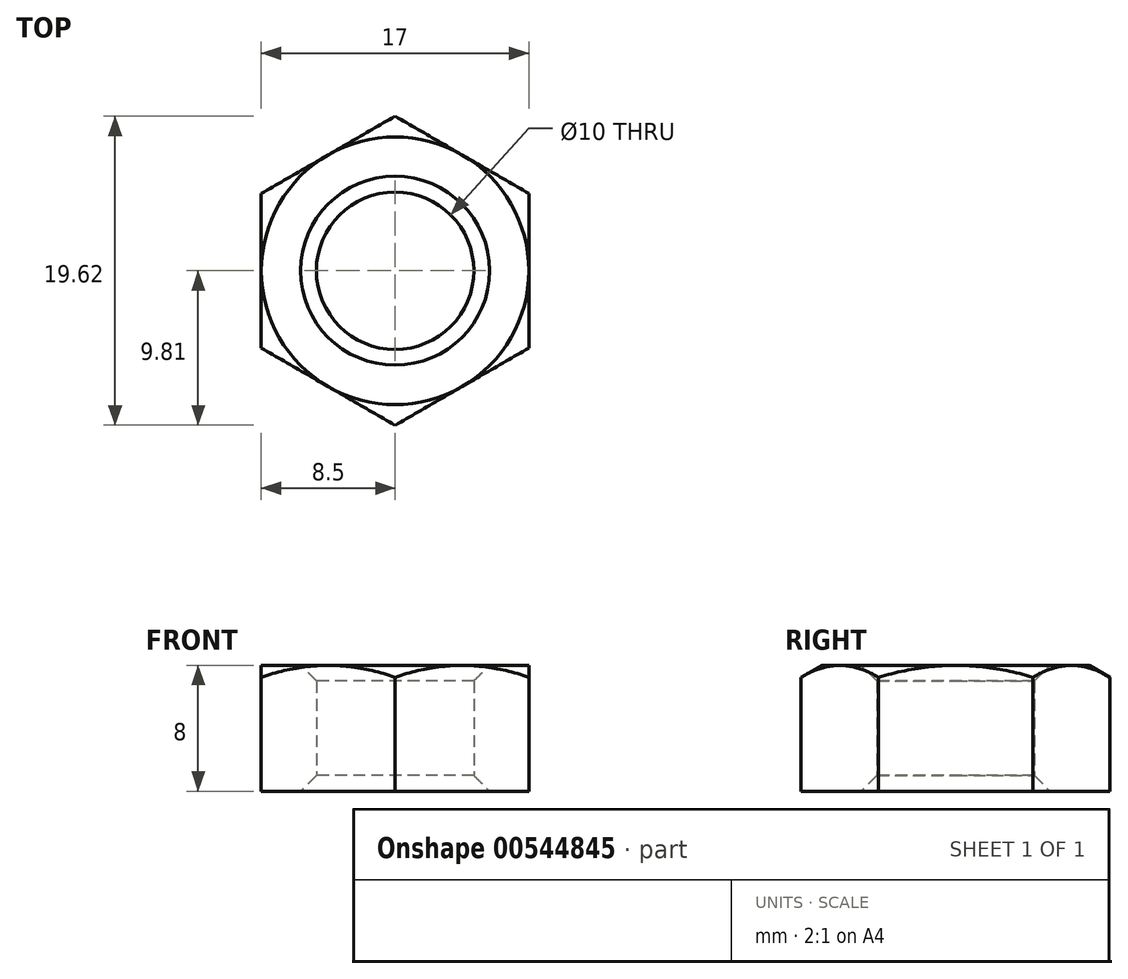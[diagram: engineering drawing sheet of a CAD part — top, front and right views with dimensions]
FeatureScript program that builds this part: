
annotation { "Feature Type Name" : "Feature", "Feature Type Description" : "" }
export const myFeature = defineFeature(function(context is Context, id is Id, definition is map)
    precondition{}
    {
        {
            var Q0;
            Q0=qCreatedBy(makeId("Top.planeOp"),FACE);
            var sketch = newSketch(context, id + "F0", { "sketchPlane" : qUnion([Q0])});
            skCircle(sketch, "E0.cCircle", {"center": v(0, 0) * mm, "radius": 8.5 * mm, "construction": true});
            skLineSegment(sketch, "E0.0", {"start": v(8.5, -4.9) * mm, "end": v(0, -9.81) * mm});
            skLineSegment(sketch, "E0.1", {"start": v(0, -9.81) * mm, "end": v(-8.5, -4.9) * mm});
            skLineSegment(sketch, "E0.2", {"start": v(-8.5, -4.9) * mm, "end": v(-8.5, 4.9) * mm});
            skLineSegment(sketch, "E0.3", {"start": v(-8.5, 4.9) * mm, "end": v(0, 9.81) * mm});
            skLineSegment(sketch, "E0.4", {"start": v(0, 9.81) * mm, "end": v(8.5, 4.9) * mm});
            skLineSegment(sketch, "E0.5", {"start": v(8.5, 4.9) * mm, "end": v(8.5, -4.9) * mm});
            skPoint(sketch, "E0.0.midPoint", {"position": v(4.25, -7.36) * mm});
            skCircle(sketch, "E1", {"center": v(0, 0) * mm, "radius": 5 * mm});
            skSolve(sketch);
        }
        {
            var Q0;
            Q0 = qSketchRegion(id + "F0", true);
            extrude(context, id + "F1", {"entities" : qUnion([Q0]), "depth" : 8 * mm, "offsetDistance" : 25 * mm});
        }
        {
            var Q0;
            Q0=makeQuery(id+"F1.opExtrude","CAP_EDGE",EDGE,{"disambiguationData":[OSD([sQuery(id+"F0.wireOp",EDGE,"E1")])],"isStart":false});
            var Q1;
            Q1=makeQuery(id+"F1.opExtrude","CAP_EDGE",EDGE,{"disambiguationData":[OSD([sQuery(id+"F0.wireOp",EDGE,"E1")])],"isStart":true});
            chamfer(context, id + "F2", {"entities" : qUnion([Q0, Q1]), "width" : 1 * mm, "tangentPropagation" : true});
        }
        {
            var Q0;
            Q0=qCreatedBy(makeId("Front.planeOp"),FACE);
            var sketch = newSketch(context, id + "F3", { "sketchPlane" : qUnion([Q0])});
            skLineSegment(sketch, "E2", {"start": v(0, 8) * mm, "end": v(0, 0) * mm, "construction": true});
            skLineSegment(sketch, "E3", {"start": v(0, 4) * mm, "end": v(8.5, 4) * mm, "construction": true});
            skLineSegment(sketch, "E4", {"start": v(8.5, 8) * mm, "end": v(18.03, 2.5) * mm});
            skLineSegment(sketch, "E5", {"start": v(18.03, 2.5) * mm, "end": v(18.03, 8) * mm});
            skLineSegment(sketch, "E6", {"start": v(18.03, 8) * mm, "end": v(8.5, 8) * mm});
            skSolve(sketch);
        }
        {
            var Q0;
            Q0 = qSketchRegion(id + "F3", true);
            var Q1;
            Q1=sQuery(id+"F3.wireOp",EDGE,"E2");
            revolve(context, id + "F4", {"operationType" : NewBodyOperationType.REMOVE, "entities" : qUnion([Q0]), "axis" : qUnion([Q1]), "revolveType" : RevolveType.FULL, "oppositeDirection" : true});
        }
    });
